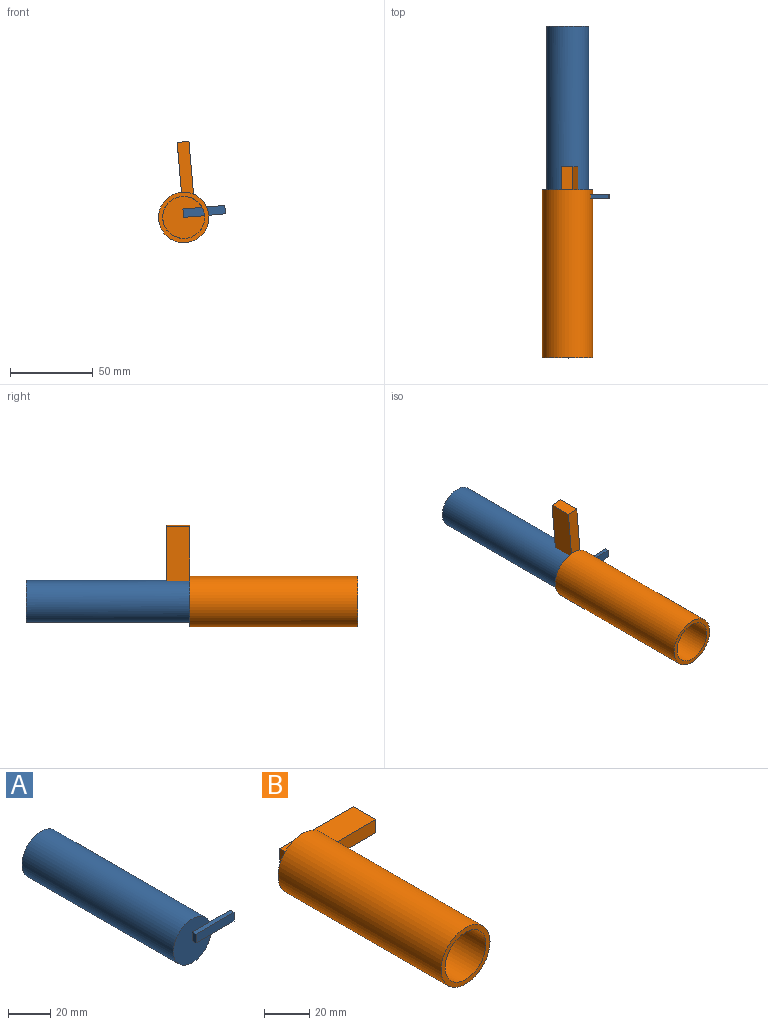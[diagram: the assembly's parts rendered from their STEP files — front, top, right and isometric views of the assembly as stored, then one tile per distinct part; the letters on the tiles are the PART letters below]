
ASSEMBLY  parts=2 mates=1
PART A: 9 faces, bbox 38.1x104.1x25.4 mm
  f0: plane 25.4x25.4mm, normal (0,-1,0), area 444mm2, adj f1,f4,f5,f6
  f1: cylinder r=12.7mm len=101.6mm, axis (0,1,0), area 8107.3mm2, adj f0,f2,f3
  f2: plane 25.4x25.4mm, normal (0,1,0), area 506.7mm2, adj f1
  f3: plane 13.76x5.08mm, normal (0,1,0), area 66.3mm2, adj f1,f4,f6,f7
  f4: plane 25.4x2.54mm, normal (0,0,1), area 64.5mm2, adj f0,f3,f5,f7,f8
  f5: plane 5.08x2.54mm, normal (-1,0,0), area 12.9mm2, adj f0,f4,f6,f8
  f6: plane 25.4x2.54mm, normal (0,0,-1), area 64.5mm2, adj f0,f3,f5,f7,f8
  f7: plane 5.08x2.54mm, normal (1,0,0), area 12.9mm2, adj f3,f4,f6,f8
  f8: plane 25.4x5.08mm, normal (0,-1,0), area 129mm2, adj f4,f5,f6,f7
PART B: 11 faces, bbox 60.8x115.6x30.5 mm
  f0: cylinder r=15.24mm len=101.6mm, axis (0,1,0), area 9728.8mm2, adj f1,f2,f9
  f1: plane 30.48x30.48mm, normal (0,-1,0), area 223mm2, adj f0,f3
  f2: plane 30.48x30.48mm, normal (0,1,0), area 624.7mm2, adj f0,f5,f6,f7
  f3: cylinder r=12.7mm len=99.06mm, axis (0,1,0), area 7904.6mm2, adj f1,f4
  f4: plane 25.4x25.4mm, normal (0,-1,0), area 506.7mm2, adj f3
  f5: plane 45.53x14mm, normal (0,0,-1), area 637.3mm2, adj f2,f6,f8,f9,f10
  f6: plane 14x7.16mm, normal (-1,0,0), area 100.2mm2, adj f2,f5,f7,f10
  f7: plane 45.53x14mm, normal (0,0,1), area 637.3mm2, adj f2,f6,f8,f9,f10
  f8: plane 14x7.16mm, normal (1,0,0), area 100.2mm2, adj f5,f7,f9,f10
  f9: plane 32.08x7.16mm, normal (0,-1,0), area 221.1mm2, adj f0,f5,f7,f8
  f10: plane 45.53x7.16mm, normal (0,1,0), area 326.1mm2, adj f5,f6,f7,f8
PLACE A rot(axis=(0,-1,0),5deg) t=(-26.25,25.52,-12.19)mm
PLACE B rot(axis=(0,-1,0),95deg) t=(-26.25,-73.54,-12.19)mm
MATE cylindrical B.f0 <-> A.f1  axis (0,-1,0) through (-26.25,-76.08,-12.19)mm
